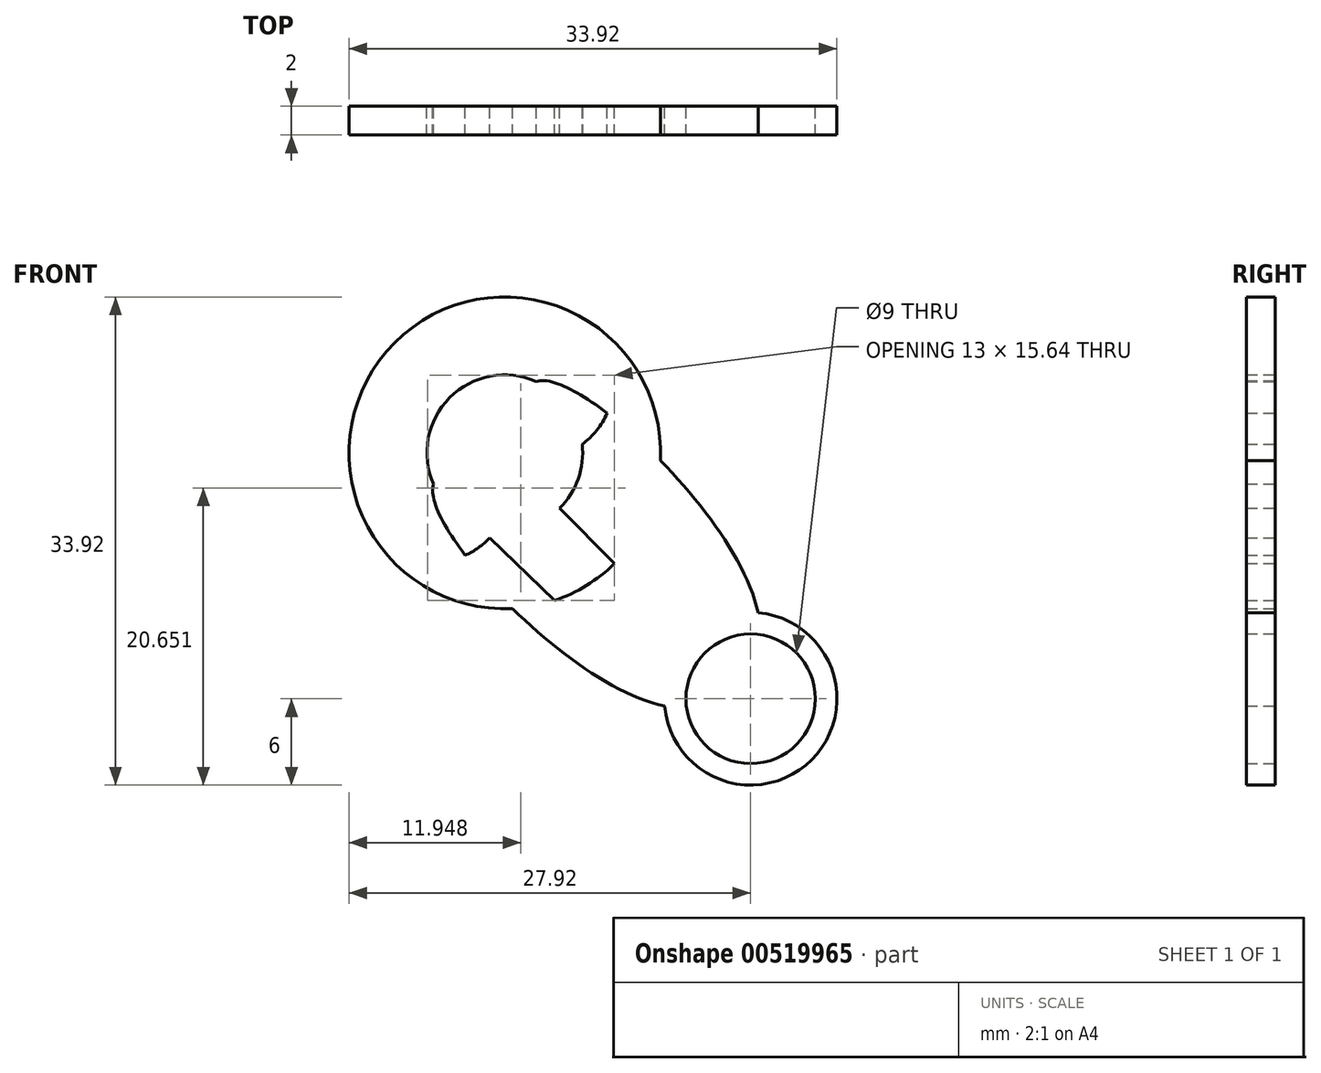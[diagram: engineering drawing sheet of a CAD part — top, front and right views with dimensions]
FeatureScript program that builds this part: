
annotation { "Feature Type Name" : "Feature", "Feature Type Description" : "" }
export const myFeature = defineFeature(function(context is Context, id is Id, definition is map)
    precondition{}
    {
        {
            var Q0;
            Q0=qCreatedBy(makeId("Front.planeOp"),FACE);
            var sketch = newSketch(context, id + "F0", { "sketchPlane" : qUnion([Q0])});
            skCircle(sketch, "E0", {"center": v(0, 0) * mm, "radius": 4.5 * mm});
            skCircle(sketch, "E1", {"center": v(0, 0) * mm, "radius": 6 * mm});
            skFitSpline(sketch, "E2", {"points": [v(-5.98, -0.51) * mm, v(-22.05, 14.92) * mm, v(-17.1, 17.1) * mm, v(-14.92, 22.05) * mm, v(0.51, 5.98) * mm, v(-5.98, -0.51) * mm]});
            skLineSegment(sketch, "E3", {"start": v(-22.05, 14.92) * mm, "end": v(-5.98, -0.51) * mm});
            skLineSegment(sketch, "E4", {"start": v(-4.3, 4.18) * mm, "end": v(-17.1, 17.1) * mm});
            skCircle(sketch, "E5", {"center": v(-22.05, 14.92) * mm, "radius": 5.42 * mm});
            skCircle(sketch, "E6", {"center": v(-17.1, 17.1) * mm, "radius": 5.42 * mm});
            skCircle(sketch, "E7", {"center": v(-14.92, 22.05) * mm, "radius": 5.42 * mm});
            skCircle(sketch, "E8", {"center": v(-17.1, 17.1) * mm, "radius": 10.83 * mm});
            skSolve(sketch);
        }
        {
            var Q0;
            Q0 = qSketchRegion(id + "F0", true);
            extrude(context, id + "F1", {"entities" : qUnion([Q0]), "depth" : 2 * mm, "offsetDistance" : 25 * mm});
        }
    });
